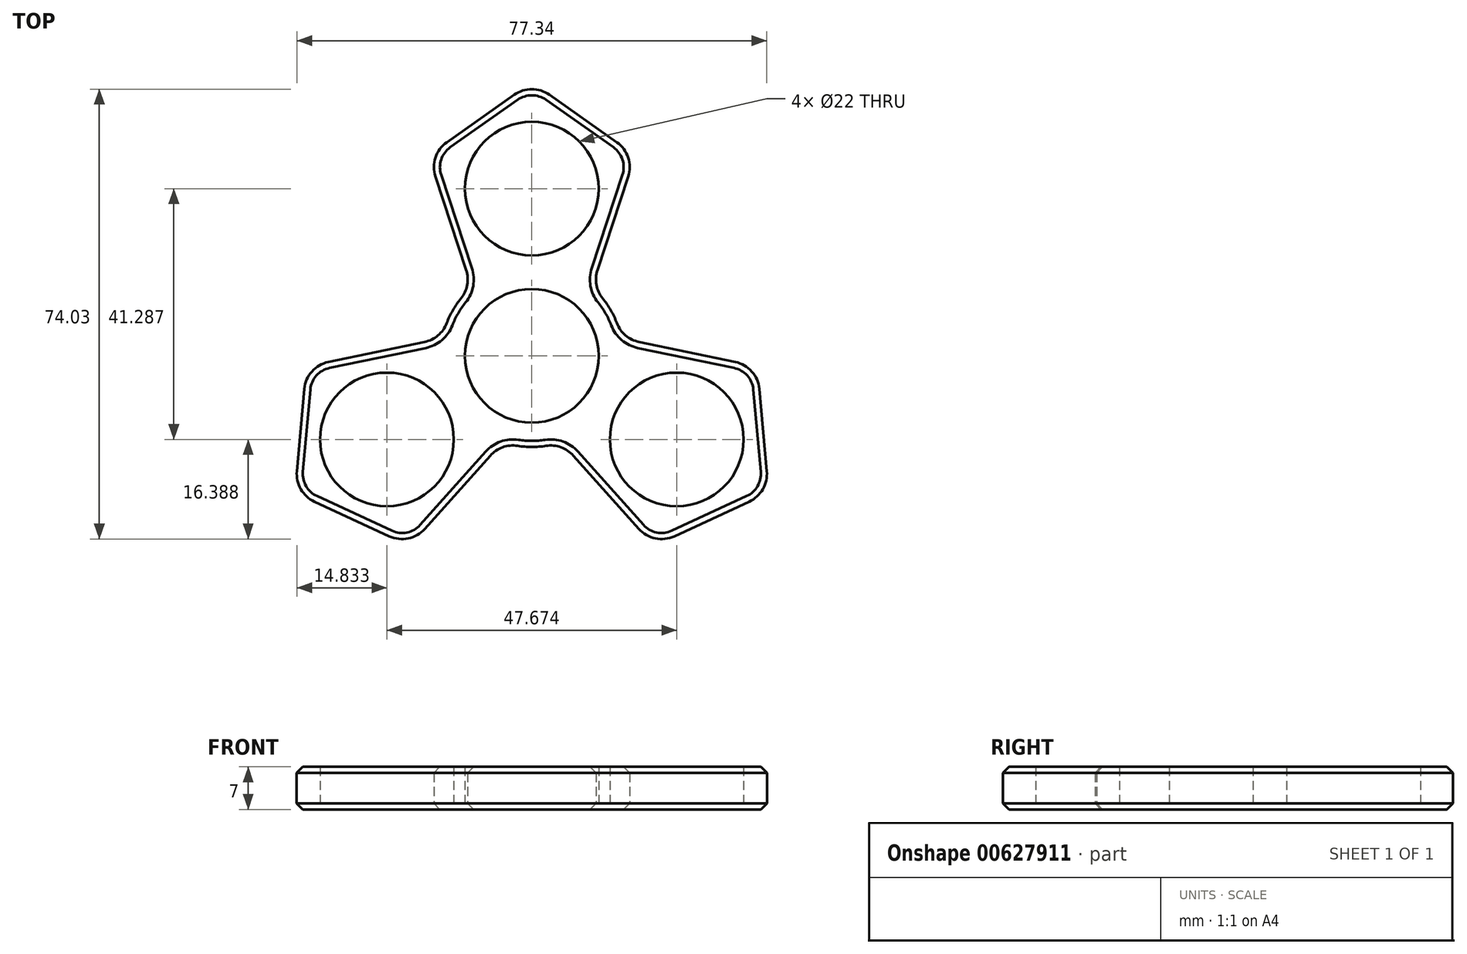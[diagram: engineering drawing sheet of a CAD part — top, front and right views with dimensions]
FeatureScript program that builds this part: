
annotation { "Feature Type Name" : "Feature", "Feature Type Description" : "" }
export const myFeature = defineFeature(function(context is Context, id is Id, definition is map)
    precondition{}
    {
        {
            var Q0;
            Q0=qCreatedBy(makeId("Top.planeOp"),FACE);
            var sketch = newSketch(context, id + "F0", { "sketchPlane" : qUnion([Q0])});
            skCircle(sketch, "E0", {"center": v(0, 0) * mm, "radius": 4 * mm});
            skCircle(sketch, "E1", {"center": v(0, 0) * mm, "radius": 11 * mm});
            skCircle(sketch, "E2", {"center": v(0, 0) * mm, "radius": 45 * mm, "construction": true});
            skCircle(sketch, "E3", {"center": v(0, 27.52) * mm, "radius": 4 * mm});
            skCircle(sketch, "E4", {"center": v(0, 27.52) * mm, "radius": 11 * mm});
            skLineSegment(sketch, "E5", {"start": v(0, 45) * mm, "end": v(-17.02, 33) * mm});
            skLineSegment(sketch, "E6", {"start": v(-17.02, 33) * mm, "end": v(-9.86, 11.3) * mm});
            skLineSegment(sketch, "E7.MirrorCS", {"start": v(0, 45) * mm, "end": v(17.02, 33) * mm});
            skLineSegment(sketch, "E8.MirrorCS", {"start": v(17.02, 33) * mm, "end": v(9.86, 11.3) * mm});
            skLineSegment(sketch, "E9.1.0", {"start": v(-38.97, -22.5) * mm, "end": v(-20.08, -31.25) * mm});
            skLineSegment(sketch, "E9.1.1", {"start": v(-20.08, -31.25) * mm, "end": v(-4.86, -14.2) * mm});
            skLineSegment(sketch, "E9.1.2", {"start": v(-38.97, -22.5) * mm, "end": v(-37.1, -1.76) * mm});
            skLineSegment(sketch, "E9.1.3", {"start": v(-37.1, -1.76) * mm, "end": v(-14.72, 2.89) * mm});
            skCircle(sketch, "E9.1.4", {"center": v(-23.84, -13.76) * mm, "radius": 11 * mm});
            skCircle(sketch, "E9.1.5", {"center": v(-23.84, -13.76) * mm, "radius": 4 * mm});
            skLineSegment(sketch, "E9.2.0", {"start": v(38.97, -22.5) * mm, "end": v(37.1, -1.76) * mm});
            skLineSegment(sketch, "E9.2.1", {"start": v(37.1, -1.76) * mm, "end": v(14.72, 2.89) * mm});
            skLineSegment(sketch, "E9.2.2", {"start": v(38.97, -22.5) * mm, "end": v(20.08, -31.25) * mm});
            skLineSegment(sketch, "E9.2.3", {"start": v(20.08, -31.25) * mm, "end": v(4.86, -14.2) * mm});
            skCircle(sketch, "E9.2.4", {"center": v(23.84, -13.76) * mm, "radius": 11 * mm});
            skCircle(sketch, "E9.2.5", {"center": v(23.84, -13.76) * mm, "radius": 4 * mm});
            skCircle(sketch, "E10", {"center": v(0, 0) * mm, "radius": 15 * mm});
            skSolve(sketch);
        }
        {
            var Q0;
            Q0=makeQuery(id+"F0.imprint","IMPRINT",FACE,{"disambiguationData":[TD([[makeQuery(id+"F0.imprint","IMPRINT",EDGE,{"derivedFrom":sQuery(id+"F0.wireOp",EDGE,"E4")}),-1.0]])]});
            var Q1;
            Q1=makeQuery(id+"F0.imprint","IMPRINT",FACE,{"disambiguationData":[TD([[makeQuery(id+"F0.imprint","IMPRINT",EDGE,{"derivedFrom":sQuery(id+"F0.wireOp",EDGE,"E9.1.0")}),1.0]])]});
            var Q2;
            Q2=makeQuery(id+"F0.imprint","IMPRINT",FACE,{"disambiguationData":[TD([[makeQuery(id+"F0.imprint","IMPRINT",EDGE,{"derivedFrom":sQuery(id+"F0.wireOp",EDGE,"E9.2.0")}),1.0]])]});
            var Q3;
            Q3=makeQuery(id+"F0.imprint","IMPRINT",FACE,{"disambiguationData":[TD([[makeQuery(id+"F0.imprint","IMPRINT",EDGE,{"derivedFrom":sQuery(id+"F0.wireOp",EDGE,"E1")}),-1.0]])]});
            extrude(context, id + "F1", {"entities" : qUnion([Q0, Q1, Q2, Q3]), "endBound" : BoundingType.SYMMETRIC, "depth" : 7 * mm, "offsetDistance" : 25 * mm});
        }
        {
            var Q0;
            Q0=makeQuery(id+"F1.opExtrude","SWEPT_EDGE",EDGE,{"disambiguationData":[OSD([sQuery(id+"F0.wireOp",EDGE,"E7.MirrorCS"),sQuery(id+"F0.wireOp",EDGE,"E8.MirrorCS")])]});
            var Q1;
            Q1=makeQuery(id+"F1.opExtrude","SWEPT_EDGE",EDGE,{"disambiguationData":[OSD([sQuery(id+"F0.wireOp",EDGE,"E8.MirrorCS"),sQuery(id+"F0.wireOp",EDGE,"E10")])]});
            var Q2;
            Q2=makeQuery(id+"F1.opExtrude","SWEPT_EDGE",EDGE,{"disambiguationData":[OSD([sQuery(id+"F0.wireOp",EDGE,"E9.2.1"),sQuery(id+"F0.wireOp",EDGE,"E10")])]});
            var Q3;
            Q3=makeQuery(id+"F1.opExtrude","SWEPT_EDGE",EDGE,{"disambiguationData":[OSD([sQuery(id+"F0.wireOp",EDGE,"E9.2.0"),sQuery(id+"F0.wireOp",EDGE,"E9.2.1")])]});
            var Q4;
            Q4=makeQuery(id+"F1.opExtrude","SWEPT_EDGE",EDGE,{"disambiguationData":[OSD([sQuery(id+"F0.wireOp",EDGE,"E9.2.0"),sQuery(id+"F0.wireOp",EDGE,"E9.2.2")])]});
            var Q5;
            Q5=makeQuery(id+"F1.opExtrude","SWEPT_EDGE",EDGE,{"disambiguationData":[OSD([sQuery(id+"F0.wireOp",EDGE,"E9.2.3"),sQuery(id+"F0.wireOp",EDGE,"E10")])]});
            var Q6;
            Q6=makeQuery(id+"F1.opExtrude","SWEPT_EDGE",EDGE,{"disambiguationData":[OSD([sQuery(id+"F0.wireOp",EDGE,"E9.2.2"),sQuery(id+"F0.wireOp",EDGE,"E9.2.3")])]});
            var Q7;
            Q7=makeQuery(id+"F1.opExtrude","SWEPT_EDGE",EDGE,{"disambiguationData":[OSD([sQuery(id+"F0.wireOp",EDGE,"E9.1.1"),sQuery(id+"F0.wireOp",EDGE,"E10")])]});
            var Q8;
            Q8=makeQuery(id+"F1.opExtrude","SWEPT_EDGE",EDGE,{"disambiguationData":[OSD([sQuery(id+"F0.wireOp",EDGE,"E9.1.0"),sQuery(id+"F0.wireOp",EDGE,"E9.1.1")])]});
            var Q9;
            Q9=makeQuery(id+"F1.opExtrude","SWEPT_EDGE",EDGE,{"disambiguationData":[OSD([sQuery(id+"F0.wireOp",EDGE,"E9.1.0"),sQuery(id+"F0.wireOp",EDGE,"E9.1.2")])]});
            var Q10;
            Q10=makeQuery(id+"F1.opExtrude","SWEPT_EDGE",EDGE,{"disambiguationData":[OSD([sQuery(id+"F0.wireOp",EDGE,"E9.1.2"),sQuery(id+"F0.wireOp",EDGE,"E9.1.3")])]});
            var Q11;
            Q11=makeQuery(id+"F1.opExtrude","SWEPT_EDGE",EDGE,{"disambiguationData":[OSD([sQuery(id+"F0.wireOp",EDGE,"E9.1.3"),sQuery(id+"F0.wireOp",EDGE,"E10")])]});
            var Q12;
            Q12=makeQuery(id+"F1.opExtrude","SWEPT_EDGE",EDGE,{"disambiguationData":[OSD([sQuery(id+"F0.wireOp",EDGE,"E6"),sQuery(id+"F0.wireOp",EDGE,"E10")])]});
            var Q13;
            Q13=makeQuery(id+"F1.opExtrude","SWEPT_EDGE",EDGE,{"disambiguationData":[OSD([sQuery(id+"F0.wireOp",EDGE,"E5"),sQuery(id+"F0.wireOp",EDGE,"E6")])]});
            var Q14;
            Q14=makeQuery(id+"F1.opExtrude","SWEPT_EDGE",EDGE,{"disambiguationData":[OSD([sQuery(id+"F0.wireOp",EDGE,"E5"),sQuery(id+"F0.wireOp",EDGE,"E7.MirrorCS")])]});
            fillet(context, id + "F2", {"entities" : qUnion([Q0, Q1, Q2, Q3, Q4, Q5, Q6, Q7, Q8, Q9, Q10, Q11, Q12, Q13, Q14]), "radius" : 5 * mm, "tangentPropagation" : true, "allowEdgeOverflow" : false});
        }
        {
            var Q0;
            Q0=makeQuery(id+"F1.opExtrude","CAP_EDGE",EDGE,{"disambiguationData":[OSD([sQuery(id+"F0.wireOp",EDGE,"E7.MirrorCS")])],"isStart":true});
            var Q1;
            Q1=makeQuery(id+"F1.opExtrude","CAP_EDGE",EDGE,{"disambiguationData":[OSD([sQuery(id+"F0.wireOp",EDGE,"E9.1.2")])],"isStart":false});
            chamfer(context, id + "F3", {"entities" : qUnion([Q0, Q1]), "width" : 1 * mm, "tangentPropagation" : true});
        }
    });
